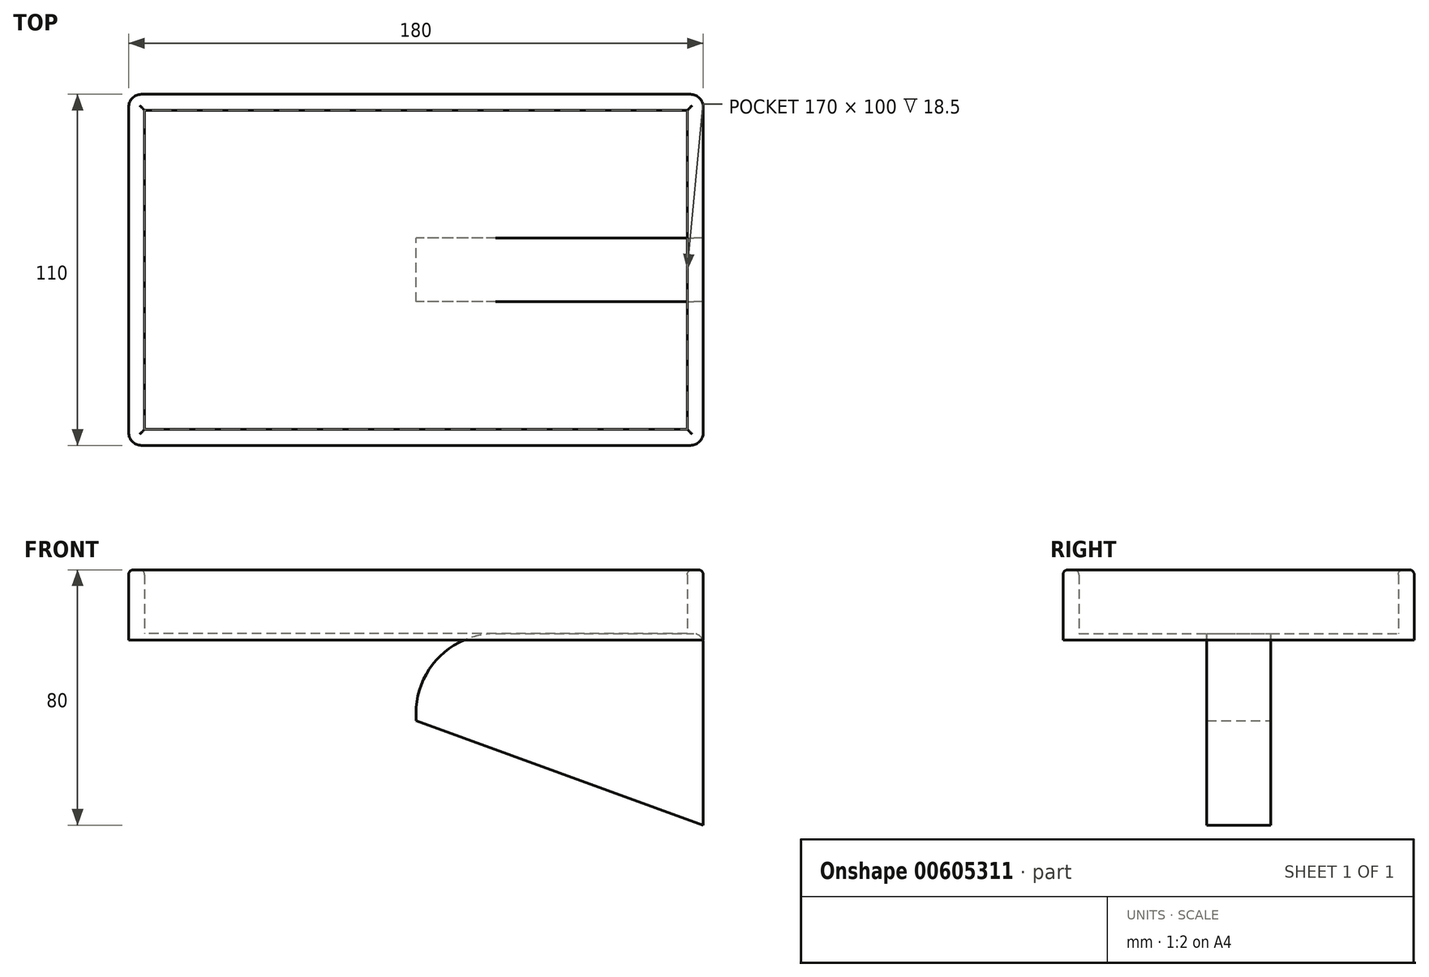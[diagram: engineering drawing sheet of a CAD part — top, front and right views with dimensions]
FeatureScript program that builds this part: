
annotation { "Feature Type Name" : "Feature", "Feature Type Description" : "" }
export const myFeature = defineFeature(function(context is Context, id is Id, definition is map)
    precondition{}
    {
        {
            var Q0;
            Q0=qCreatedBy(makeId("Top.planeOp"),FACE);
            var sketch = newSketch(context, id + "F0", { "sketchPlane" : qUnion([Q0])});
            skLineSegment(sketch, "E0.bottom", {"start": v(85, -50) * mm, "end": v(-85, -50) * mm});
            skLineSegment(sketch, "E0.top", {"start": v(85, 50) * mm, "end": v(-85, 50) * mm});
            skLineSegment(sketch, "E0.left", {"start": v(85, -50) * mm, "end": v(85, 50) * mm});
            skLineSegment(sketch, "E0.right", {"start": v(-85, -50) * mm, "end": v(-85, 50) * mm});
            skPoint(sketch, "E0.middle", {"position": v(0, 0) * mm});
            skLineSegment(sketch, "E1.0", {"start": v(-90, -51) * mm, "end": v(-90, 51) * mm});
            skLineSegment(sketch, "E1.1", {"start": v(86, -55) * mm, "end": v(-86, -55) * mm});
            skLineSegment(sketch, "E1.2", {"start": v(90, -51) * mm, "end": v(90, 51) * mm});
            skLineSegment(sketch, "E1.3", {"start": v(86, 55) * mm, "end": v(-86, 55) * mm});
            skPoint(sketch, "E2.visualSharp", {"position": v(-90, 55) * mm});
            skArc(sketch, "E2.filletArc", {"start": v(-86, 55) * mm, "mid": v(-88.83, 53.83) * mm, "end": v(-90, 51) * mm});
            skPoint(sketch, "E3.visualSharp", {"position": v(90, 55) * mm});
            skArc(sketch, "E3.filletArc", {"start": v(90, 51) * mm, "mid": v(88.83, 53.83) * mm, "end": v(86, 55) * mm});
            skPoint(sketch, "E4.visualSharp", {"position": v(90, -55) * mm});
            skArc(sketch, "E4.filletArc", {"start": v(86, -55) * mm, "mid": v(88.83, -53.83) * mm, "end": v(90, -51) * mm});
            skPoint(sketch, "E5.visualSharp", {"position": v(-90, -55) * mm});
            skArc(sketch, "E5.filletArc", {"start": v(-90, -51) * mm, "mid": v(-88.83, -53.83) * mm, "end": v(-86, -55) * mm});
            skSolve(sketch);
        }
        {
            var Q0;
            Q0=makeQuery(id+"F0.imprint","IMPRINT",FACE,{"disambiguationData":[TD([[makeQuery(id+"F0.imprint","IMPRINT",EDGE,{"derivedFrom":sQuery(id+"F0.wireOp",EDGE,"E0.bottom")}),1.0]])]});
            extrude(context, id + "F1", {"entities" : qUnion([Q0]), "depth" : 20 * mm, "offsetDistance" : 25 * mm});
        }
        {
            var Q0;
            Q0=makeQuery(id+"F0.imprint","IMPRINT",FACE,{"disambiguationData":[TD([[makeQuery(id+"F0.imprint","IMPRINT",EDGE,{"derivedFrom":sQuery(id+"F0.wireOp",EDGE,"E0.bottom")}),1.0]])]});
            var Q1;
            Q1=makeQuery(id+"F0.imprint","IMPRINT",FACE,{"disambiguationData":[TD([[makeQuery(id+"F0.imprint","IMPRINT",EDGE,{"derivedFrom":sQuery(id+"F0.wireOp",EDGE,"E0.bottom")}),-1.0]])]});
            extrude(context, id + "F2", {"entities" : qUnion([Q0, Q1]), "operationType" : NewBodyOperationType.ADD, "oppositeDirection" : true, "depth" : 2 * mm, "offsetDistance" : 25 * mm});
        }
        {
            var Q0;
            Q0=makeQuery(id+"F1.opExtrude","CAP_EDGE",EDGE,{"disambiguationData":[OSD([sQuery(id+"F0.wireOp",EDGE,"E1.1")])],"isStart":false});
            var Q1;
            Q1=makeQuery(id+"F1.opExtrude","CAP_EDGE",EDGE,{"disambiguationData":[OSD([sQuery(id+"F0.wireOp",EDGE,"E0.bottom")])],"isStart":false});
            var Q2;
            Q2=makeQuery(id+"F1.opExtrude","CAP_EDGE",EDGE,{"disambiguationData":[OSD([sQuery(id+"F0.wireOp",EDGE,"E0.right")])],"isStart":false});
            var Q3;
            Q3=makeQuery(id+"F1.opExtrude","CAP_EDGE",EDGE,{"disambiguationData":[OSD([sQuery(id+"F0.wireOp",EDGE,"E1.0")])],"isStart":false});
            var Q4;
            Q4=makeQuery(id+"F1.opExtrude","CAP_EDGE",EDGE,{"disambiguationData":[OSD([sQuery(id+"F0.wireOp",EDGE,"E0.top")])],"isStart":false});
            var Q5;
            Q5=makeQuery(id+"F1.opExtrude","CAP_EDGE",EDGE,{"disambiguationData":[OSD([sQuery(id+"F0.wireOp",EDGE,"E1.3")])],"isStart":false});
            var Q6;
            Q6=makeQuery(id+"F1.opExtrude","CAP_EDGE",EDGE,{"disambiguationData":[OSD([sQuery(id+"F0.wireOp",EDGE,"E1.2")])],"isStart":false});
            var Q7;
            Q7=makeQuery(id+"F1.opExtrude","CAP_EDGE",EDGE,{"disambiguationData":[OSD([sQuery(id+"F0.wireOp",EDGE,"E0.left")])],"isStart":false});
            fillet(context, id + "F3", {"entities" : qUnion([Q0, Q1, Q2, Q3, Q4, Q5, Q6, Q7]), "radius" : 1.5 * mm, "tangentPropagation" : true, "allowEdgeOverflow" : false});
        }
        {
            var Q0;
            Q0=qCreatedBy(makeId("Front.planeOp"),FACE);
            var sketch = newSketch(context, id + "F4", { "sketchPlane" : qUnion([Q0])});
            skLineSegment(sketch, "E6", {"start": v(25, 0) * mm, "end": v(87, 0) * mm});
            skLineSegment(sketch, "E7", {"start": v(90, -3) * mm, "end": v(90, -60) * mm});
            skLineSegment(sketch, "E8", {"start": v(90, -60) * mm, "end": v(0, -27.24) * mm});
            skLineSegment(sketch, "E9", {"start": v(0, -27.24) * mm, "end": v(0, -25) * mm});
            skPoint(sketch, "E10.visualSharp", {"position": v(0, 0) * mm});
            skArc(sketch, "E10.filletArc", {"start": v(25, 0) * mm, "mid": v(7.32, -7.32) * mm, "end": v(0, -25) * mm});
            skPoint(sketch, "E11.visualSharp", {"position": v(90, 0) * mm});
            skArc(sketch, "E11.filletArc", {"start": v(90, -3) * mm, "mid": v(89.12, -0.88) * mm, "end": v(87, 0) * mm});
            skSolve(sketch);
        }
        {
            var Q0;
            Q0=makeQuery(id+"F4.imprint","IMPRINT",FACE,{"disambiguationData":[TD([[makeQuery(id+"F4.imprint","IMPRINT",EDGE,{"derivedFrom":sQuery(id+"F4.wireOp",EDGE,"E6")}),-1.0]])]});
            extrude(context, id + "F5", {"entities" : qUnion([Q0]), "endBound" : BoundingType.SYMMETRIC, "depth" : 20 * mm, "offsetDistance" : 25 * mm});
        }
    });
